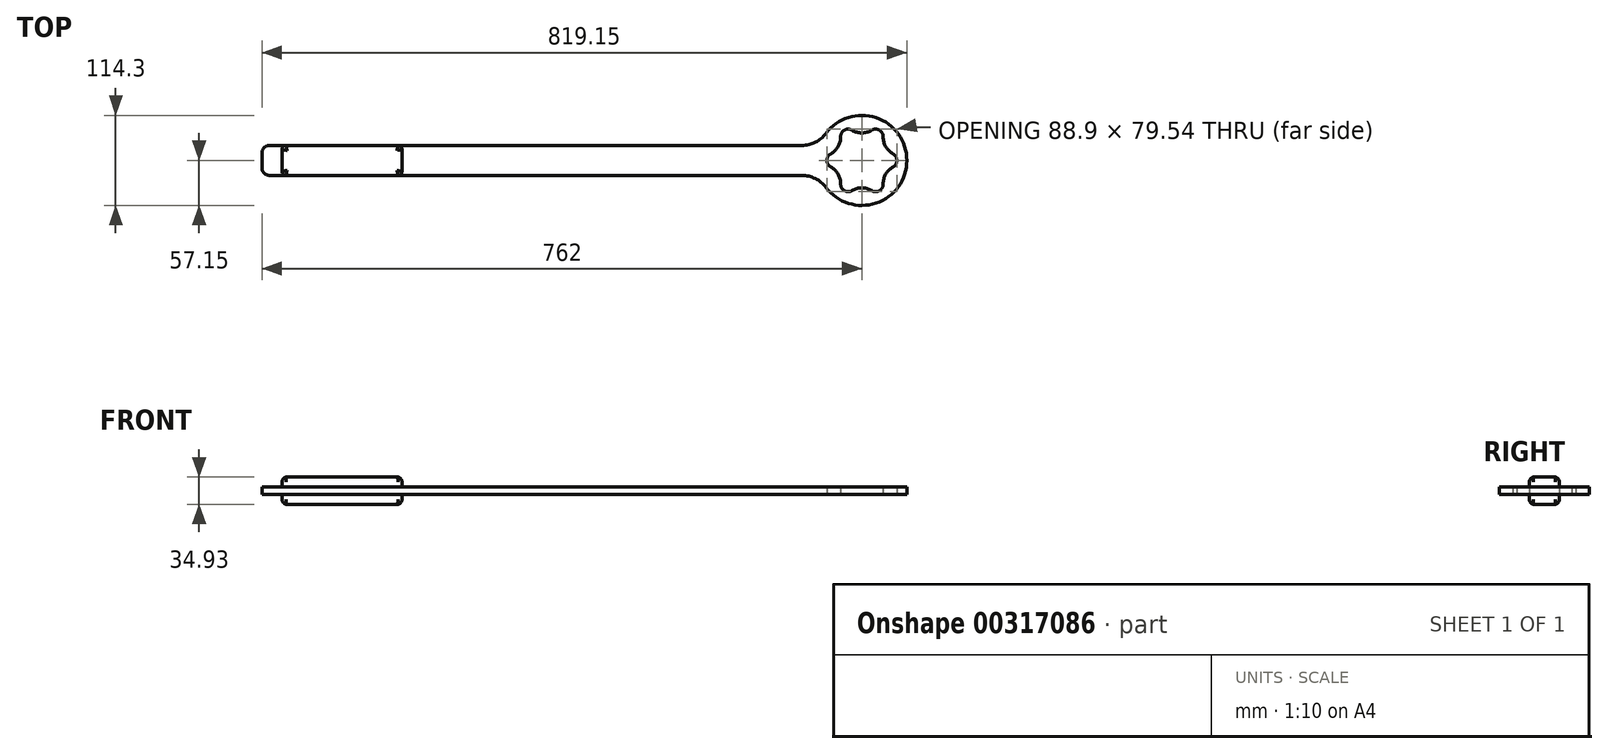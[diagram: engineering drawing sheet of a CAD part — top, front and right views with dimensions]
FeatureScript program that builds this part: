
annotation { "Feature Type Name" : "Feature", "Feature Type Description" : "" }
export const myFeature = defineFeature(function(context is Context, id is Id, definition is map)
    precondition{}
    {
        {
            var Q0;
            Q0=qCreatedBy(makeId("Top.planeOp"),FACE);
            var sketch = newSketch(context, id + "F0", { "sketchPlane" : qUnion([Q0])});
            skCircle(sketch, "E0", {"center": v(0, 0) * mm, "radius": 44.45 * mm, "construction": true});
            skCircle(sketch, "E1", {"center": v(0, 0) * mm, "radius": 34.93 * mm, "construction": true});
            skArc(sketch, "E2", {"start": v(-39.54, 8.33) * mm, "mid": v(-44.45, 0) * mm, "end": v(-39.54, -8.33) * mm});
            skArc(sketch, "E3", {"start": v(-39.54, -8.33) * mm, "mid": v(-30.25, -17.46) * mm, "end": v(-26.99, -30.08) * mm});
            skArc(sketch, "E4", {"start": v(-26.99, -30.08) * mm, "mid": v(-22.22, -38.5) * mm, "end": v(-12.55, -38.4) * mm});
            skArc(sketch, "E5", {"start": v(-12.55, -38.4) * mm, "mid": v(0, -34.93) * mm, "end": v(12.55, -38.4) * mm});
            skArc(sketch, "E6", {"start": v(12.55, -38.4) * mm, "mid": v(22.22, -38.5) * mm, "end": v(26.99, -30.08) * mm});
            skArc(sketch, "E7", {"start": v(26.99, -30.08) * mm, "mid": v(30.25, -17.46) * mm, "end": v(39.54, -8.33) * mm});
            skArc(sketch, "E8", {"start": v(39.54, -8.33) * mm, "mid": v(44.45, 0) * mm, "end": v(39.54, 8.33) * mm});
            skArc(sketch, "E9", {"start": v(39.54, 8.33) * mm, "mid": v(30.25, 17.46) * mm, "end": v(26.99, 30.08) * mm});
            skArc(sketch, "E10", {"start": v(26.99, 30.08) * mm, "mid": v(22.22, 38.5) * mm, "end": v(12.55, 38.4) * mm});
            skArc(sketch, "E11", {"start": v(12.55, 38.4) * mm, "mid": v(0, 34.93) * mm, "end": v(-12.55, 38.4) * mm});
            skArc(sketch, "E12", {"start": v(-12.55, 38.4) * mm, "mid": v(-22.22, 38.5) * mm, "end": v(-26.99, 30.08) * mm});
            skArc(sketch, "E13", {"start": v(-26.99, 30.08) * mm, "mid": v(-30.25, 17.46) * mm, "end": v(-39.54, 8.33) * mm});
            skLineSegment(sketch, "E14", {"start": v(-57.15, 0) * mm, "end": v(57.15, 0) * mm, "construction": true});
            skArc(sketch, "E15", {"start": v(-45.72, -34.29) * mm, "mid": v(57.15, 0) * mm, "end": v(-45.72, 34.3) * mm});
            skLineSegment(sketch, "E16.bottom", {"start": v(-76.2, 19.05) * mm, "end": v(-752.48, 19.05) * mm});
            skLineSegment(sketch, "E16.top", {"start": v(-76.2, -19.05) * mm, "end": v(-752.48, -19.05) * mm});
            skLineSegment(sketch, "E16.right", {"start": v(-762, 9.52) * mm, "end": v(-762, -9.53) * mm});
            skPoint(sketch, "E17.visualSharp", {"position": v(-53.88, -19.05) * mm});
            skArc(sketch, "E17.filletArc", {"start": v(-45.72, -34.29) * mm, "mid": v(-59.16, -23.07) * mm, "end": v(-76.2, -19.05) * mm});
            skPoint(sketch, "E18.visualSharp", {"position": v(-53.88, 19.05) * mm});
            skArc(sketch, "E18.filletArc", {"start": v(-76.2, 19.05) * mm, "mid": v(-59.16, 23.07) * mm, "end": v(-45.72, 34.29) * mm});
            skPoint(sketch, "E19.visualSharp", {"position": v(-762, -19.05) * mm});
            skArc(sketch, "E19.filletArc", {"start": v(-762, -9.53) * mm, "mid": v(-759.21, -16.26) * mm, "end": v(-752.48, -19.05) * mm});
            skPoint(sketch, "E20.visualSharp", {"position": v(-762, 19.05) * mm});
            skArc(sketch, "E20.filletArc", {"start": v(-752.48, 19.05) * mm, "mid": v(-759.21, 16.26) * mm, "end": v(-762, 9.52) * mm});
            skSolve(sketch);
        }
        {
            var Q0;
            Q0 = qSketchRegion(id + "F0", true);
            extrude(context, id + "F1", {"entities" : qUnion([Q0]), "depth" : 9.52 * mm});
        }
        {
            var Q0;
            Q0=makeQuery(id+"F1.opExtrude","CAP_FACE",FACE,{"disambiguationData":[OSD([sQuery(id+"F0.wireOp",EDGE,"E2"),sQuery(id+"F0.wireOp",EDGE,"E3"),sQuery(id+"F0.wireOp",EDGE,"E4"),sQuery(id+"F0.wireOp",EDGE,"E5"),sQuery(id+"F0.wireOp",EDGE,"E6"),sQuery(id+"F0.wireOp",EDGE,"E7"),sQuery(id+"F0.wireOp",EDGE,"E8"),sQuery(id+"F0.wireOp",EDGE,"E9"),sQuery(id+"F0.wireOp",EDGE,"E10"),sQuery(id+"F0.wireOp",EDGE,"E11"),sQuery(id+"F0.wireOp",EDGE,"E12"),sQuery(id+"F0.wireOp",EDGE,"E13"),sQuery(id+"F0.wireOp",EDGE,"E15"),sQuery(id+"F0.wireOp",EDGE,"E16.bottom"),sQuery(id+"F0.wireOp",EDGE,"E16.top"),sQuery(id+"F0.wireOp",EDGE,"E16.right"),sQuery(id+"F0.wireOp",EDGE,"E17.filletArc"),sQuery(id+"F0.wireOp",EDGE,"E18.filletArc"),sQuery(id+"F0.wireOp",EDGE,"E19.filletArc"),sQuery(id+"F0.wireOp",EDGE,"E20.filletArc")])],"isStart":false});
            var sketch = newSketch(context, id + "F2", { "sketchPlane" : qUnion([Q0])});
            skLineSegment(sketch, "E21.bottom", {"start": v(-736.6, 19.05) * mm, "end": v(-584.2, 19.05) * mm});
            skLineSegment(sketch, "E21.top", {"start": v(-736.6, -19.05) * mm, "end": v(-584.2, -19.05) * mm});
            skLineSegment(sketch, "E21.left", {"start": v(-736.6, 19.05) * mm, "end": v(-736.6, -19.05) * mm});
            skLineSegment(sketch, "E21.right", {"start": v(-584.2, 19.05) * mm, "end": v(-584.2, -19.05) * mm});
            skSolve(sketch);
        }
        {
            var Q0;
            Q0 = qSketchRegion(id + "F2", true);
            extrude(context, id + "F3", {"entities" : qUnion([Q0]), "depth" : 12.7 * mm});
        }
        {
            var Q0;
            Q0=makeQuery(id+"F1.opExtrude","CAP_FACE",FACE,{"disambiguationData":[OSD([sQuery(id+"F0.wireOp",EDGE,"E2"),sQuery(id+"F0.wireOp",EDGE,"E3"),sQuery(id+"F0.wireOp",EDGE,"E4"),sQuery(id+"F0.wireOp",EDGE,"E5"),sQuery(id+"F0.wireOp",EDGE,"E6"),sQuery(id+"F0.wireOp",EDGE,"E7"),sQuery(id+"F0.wireOp",EDGE,"E8"),sQuery(id+"F0.wireOp",EDGE,"E9"),sQuery(id+"F0.wireOp",EDGE,"E10"),sQuery(id+"F0.wireOp",EDGE,"E11"),sQuery(id+"F0.wireOp",EDGE,"E12"),sQuery(id+"F0.wireOp",EDGE,"E13"),sQuery(id+"F0.wireOp",EDGE,"E15"),sQuery(id+"F0.wireOp",EDGE,"E16.bottom"),sQuery(id+"F0.wireOp",EDGE,"E16.top"),sQuery(id+"F0.wireOp",EDGE,"E16.right"),sQuery(id+"F0.wireOp",EDGE,"E17.filletArc"),sQuery(id+"F0.wireOp",EDGE,"E18.filletArc"),sQuery(id+"F0.wireOp",EDGE,"E19.filletArc"),sQuery(id+"F0.wireOp",EDGE,"E20.filletArc")])],"isStart":true});
            var sketch = newSketch(context, id + "F4", { "sketchPlane" : qUnion([Q0])});
            skLineSegment(sketch, "E22.0", {"start": v(-736.6, -19.05) * mm, "end": v(-584.2, -19.05) * mm});
            skLineSegment(sketch, "E22.1", {"start": v(-736.6, 19.05) * mm, "end": v(-584.2, 19.05) * mm});
            skLineSegment(sketch, "E22.2", {"start": v(-736.6, -19.05) * mm, "end": v(-736.6, 19.05) * mm});
            skLineSegment(sketch, "E22.3", {"start": v(-584.2, -19.05) * mm, "end": v(-584.2, 19.05) * mm});
            skSolve(sketch);
        }
        {
            var Q0;
            Q0 = qSketchRegion(id + "F4", true);
            extrude(context, id + "F5", {"entities" : qUnion([Q0]), "depth" : 12.7 * mm});
        }
        {
            var Q0;
            Q0=makeQuery(id+"F3.opExtrude","CAP_FACE",FACE,{"disambiguationData":[OSD([sQuery(id+"F2.wireOp",EDGE,"E21.bottom"),sQuery(id+"F2.wireOp",EDGE,"E21.top"),sQuery(id+"F2.wireOp",EDGE,"E21.left"),sQuery(id+"F2.wireOp",EDGE,"E21.right")])],"isStart":false});
            var Q1;
            Q1=makeQuery(id+"F5.opExtrude","CAP_FACE",FACE,{"disambiguationData":[OSD([sQuery(id+"F4.wireOp",EDGE,"E22.0"),sQuery(id+"F4.wireOp",EDGE,"E22.1"),sQuery(id+"F4.wireOp",EDGE,"E22.2"),sQuery(id+"F4.wireOp",EDGE,"E22.3")])],"isStart":false});
            fillet(context, id + "F6", {"entities" : qUnion([Q0, Q1]), "radius" : 6.35 * mm, "tangentPropagation" : true, "allowEdgeOverflow" : false});
        }
        {
            var Q0;
            Q0=makeQuery(id+"F6.opFillet","BLEND_EDGE",EDGE,{"blendedFrom":[makeQuery(id+"F3.opExtrude","CAP_EDGE",EDGE,{"disambiguationData":[OSD([sQuery(id+"F2.wireOp",EDGE,"E21.top")])],"isStart":false}),makeQuery(id+"F3.opExtrude","CAP_EDGE",EDGE,{"disambiguationData":[OSD([sQuery(id+"F2.wireOp",EDGE,"E21.left")])],"isStart":false})],"blendedInto":[]});
            var Q1;
            Q1=makeQuery(id+"F6.opFillet","BLEND_EDGE",EDGE,{"blendedFrom":[makeQuery(id+"F3.opExtrude","CAP_EDGE",EDGE,{"disambiguationData":[OSD([sQuery(id+"F2.wireOp",EDGE,"E21.top")])],"isStart":false}),makeQuery(id+"F3.opExtrude","CAP_EDGE",EDGE,{"disambiguationData":[OSD([sQuery(id+"F2.wireOp",EDGE,"E21.right")])],"isStart":false})],"blendedInto":[]});
            var Q2;
            Q2=makeQuery(id+"F6.opFillet","BLEND_EDGE",EDGE,{"blendedFrom":[makeQuery(id+"F3.opExtrude","CAP_EDGE",EDGE,{"disambiguationData":[OSD([sQuery(id+"F2.wireOp",EDGE,"E21.bottom")])],"isStart":false}),makeQuery(id+"F3.opExtrude","CAP_EDGE",EDGE,{"disambiguationData":[OSD([sQuery(id+"F2.wireOp",EDGE,"E21.right")])],"isStart":false})],"blendedInto":[]});
            var Q3;
            Q3=makeQuery(id+"F6.opFillet","BLEND_EDGE",EDGE,{"blendedFrom":[makeQuery(id+"F3.opExtrude","CAP_EDGE",EDGE,{"disambiguationData":[OSD([sQuery(id+"F2.wireOp",EDGE,"E21.bottom")])],"isStart":false}),makeQuery(id+"F3.opExtrude","CAP_EDGE",EDGE,{"disambiguationData":[OSD([sQuery(id+"F2.wireOp",EDGE,"E21.left")])],"isStart":false})],"blendedInto":[]});
            var Q4;
            Q4=makeQuery(id+"F6.opFillet","BLEND_EDGE",EDGE,{"blendedFrom":[makeQuery(id+"F5.opExtrude","CAP_EDGE",EDGE,{"disambiguationData":[OSD([sQuery(id+"F4.wireOp",EDGE,"E22.0")])],"isStart":false}),makeQuery(id+"F5.opExtrude","CAP_EDGE",EDGE,{"disambiguationData":[OSD([sQuery(id+"F4.wireOp",EDGE,"E22.2")])],"isStart":false})],"blendedInto":[]});
            var Q5;
            Q5=makeQuery(id+"F6.opFillet","BLEND_EDGE",EDGE,{"blendedFrom":[makeQuery(id+"F5.opExtrude","CAP_EDGE",EDGE,{"disambiguationData":[OSD([sQuery(id+"F4.wireOp",EDGE,"E22.1")])],"isStart":false}),makeQuery(id+"F5.opExtrude","CAP_EDGE",EDGE,{"disambiguationData":[OSD([sQuery(id+"F4.wireOp",EDGE,"E22.2")])],"isStart":false})],"blendedInto":[]});
            var Q6;
            Q6=makeQuery(id+"F6.opFillet","BLEND_EDGE",EDGE,{"blendedFrom":[makeQuery(id+"F5.opExtrude","CAP_EDGE",EDGE,{"disambiguationData":[OSD([sQuery(id+"F4.wireOp",EDGE,"E22.0")])],"isStart":false}),makeQuery(id+"F5.opExtrude","CAP_EDGE",EDGE,{"disambiguationData":[OSD([sQuery(id+"F4.wireOp",EDGE,"E22.3")])],"isStart":false})],"blendedInto":[]});
            var Q7;
            Q7=makeQuery(id+"F6.opFillet","BLEND_EDGE",EDGE,{"blendedFrom":[makeQuery(id+"F5.opExtrude","CAP_EDGE",EDGE,{"disambiguationData":[OSD([sQuery(id+"F4.wireOp",EDGE,"E22.1")])],"isStart":false}),makeQuery(id+"F5.opExtrude","CAP_EDGE",EDGE,{"disambiguationData":[OSD([sQuery(id+"F4.wireOp",EDGE,"E22.3")])],"isStart":false})],"blendedInto":[]});
            fillet(context, id + "F7", {"entities" : qUnion([Q0, Q1, Q2, Q3, Q4, Q5, Q6, Q7]), "radius" : 5.08 * mm, "tangentPropagation" : true, "allowEdgeOverflow" : false});
        }
    });
